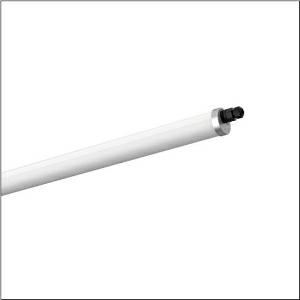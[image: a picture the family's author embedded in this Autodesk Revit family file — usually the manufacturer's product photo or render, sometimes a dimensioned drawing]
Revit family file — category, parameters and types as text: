
# Revit family: monsun_31_tube_51ft10dn460a
name_source: partatom
category: Lighting Fixtures
units: mm (PartAtom-declared; Revit-internal decimal feet)

## family parameters
Cut with Voids When Loaded = No
Host = Face
Light Source = No
Part Type = Normal
Room Calculation Point = No
Round Connector Dimension = Use Diameter
Shared = No

## types (1)
- Monsun 31 Tube (1 x LED, 6500 lm, 40 W, 4000K)
    Apparent Load = 40 VA
    CIE Flux Codes = 42 71 90 91 100
    Color Rendering = 80
    Color Temperature = 4000K
    Default Elevation = 1800 mm
    Description = Monsun 31 Tube, tubular luminaire, primary optical cover: diffuser, of PMMA, light emission: direct distribution, primary light characteristic: symmetric, installation type: suspended mounting, surface-mounted, LED, rated luminous flux: 6.500lm, luminous efficacy: 160lm/W, light colour: 840, colour temperature: 4000K, control gear: DALI 2, with with 1 terminal, 5-pole, max. 2.5mm², through-wiring: 5x 1.5mm², mains connection: 220..240V, AC, 50/60Hz, rated input power: 40W, housing, cylindrical, of PMMA, semi-transparent, matt white, with luminaire and ceiling fastening, V4A, mounting with brackets of stainless steel, length: 1.570mm, diameter: 75mm, end cap, of stainless steel (V4A), protection rating (complete): IP67/IP69K, insulation class (complete): insulation class I (protective earthing), certification: CE, UKCA, impact resistance: IK07, permissible operating ambient temperature: -20..+40°C, corresponds to IFS (International Featured Standards) requirements for safety and quality in the food industry, usage in unprotected outdoor areas possible with horizontal mounting, contact your sales advisor before using the luminaires in applications with unclear chemical exposure, large temperature fluctuations or condensation-forming humidity, packaging unit: 1 piece
    Height = 83 mm
    Lamp = 1 x LED
    Lamp Light Flux = 6500 lm
    Lamp Power = 40 W
    Lamp count = 1
    Length = 1570 mm
    Luminous efficacy = 163 lm/W
    Manufacturer = Siteco
    ModVariant = No
    Model = 51FT10DN460A
    Mounting Place = Ceiling
    Mounting Type = Pendant
    Number of Poles = 1
    OnlyDefault = Yes
    Power Factor = 1
    Product Name = Monsun 31 Tube
    Product group = tubular luminaire
    ProductGroupID = 906
    Protection Class = Protection class I
    RLX_Detail_Level = 1
    RLX_Emergency_Light_Flux = 0 lm
    RLX_Emergency_Type = 0
    RLX_Emergency_Type_DB = No
    RlxData = <blob elided: 25261 chars, md5=807dd315>
    Socket = socket
    Standby Power = 0 W
    System Light Flux = 6500 lm
    System Power = 40 W
    Type Comments = Product without accessories
    Type Image = l_1228461.jpg
    URL = http://relux.com
    VarID = ---
    Voltage = 0 V
    Weight = 0.00 kg
    Width = 75 mm

## geometry (parser evidence)
native form markers: Blend x4, Sweep x15
no freeform markers — native parametric forms only
